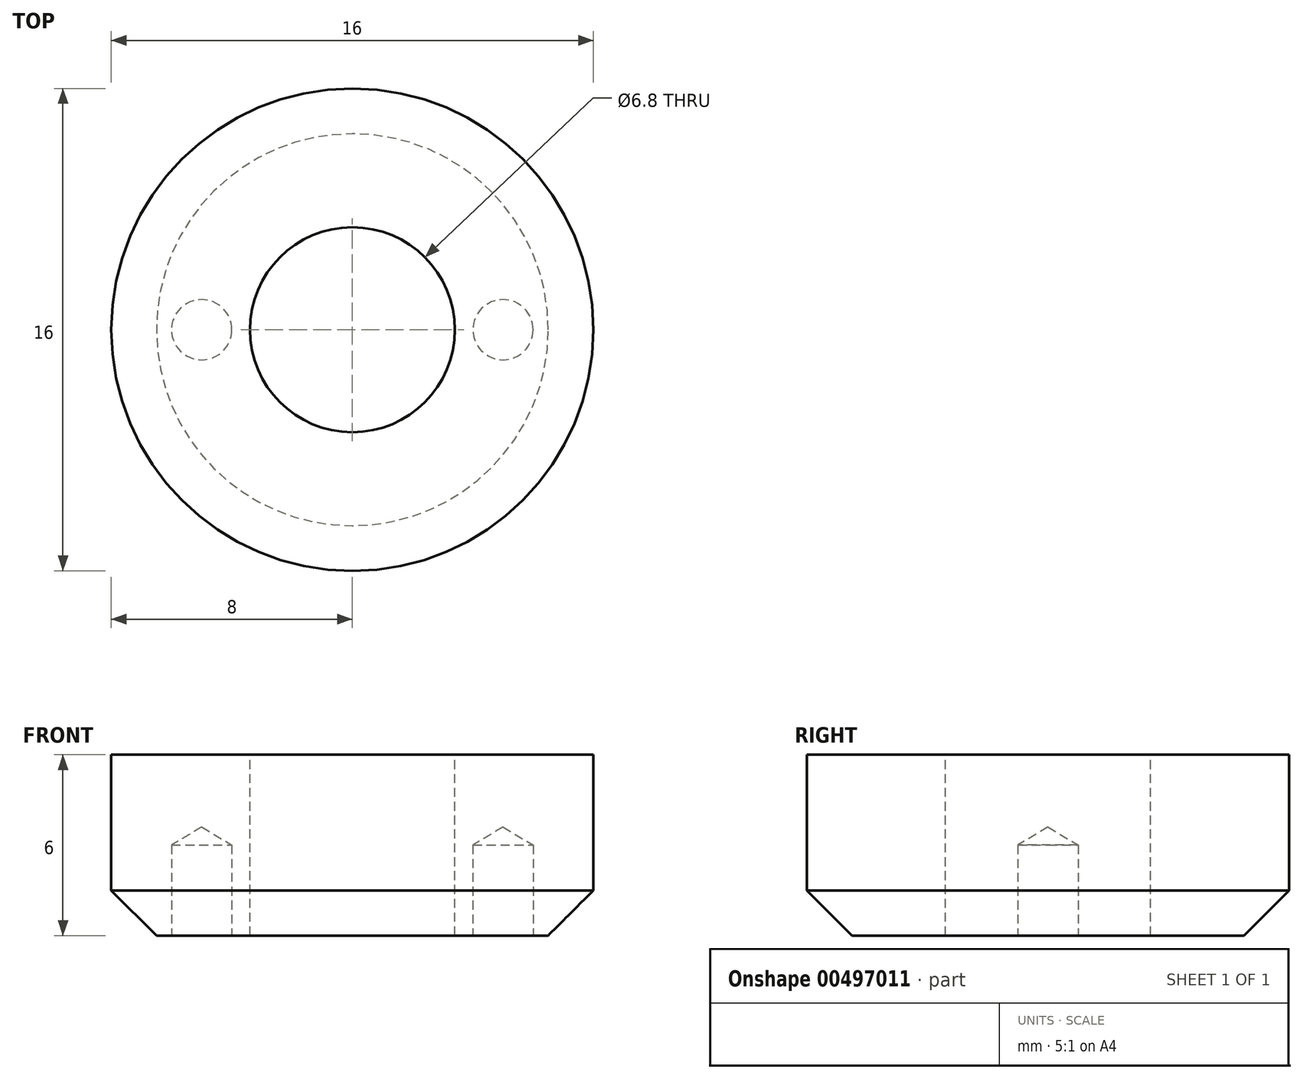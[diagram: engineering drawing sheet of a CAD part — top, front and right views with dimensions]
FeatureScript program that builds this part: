
annotation { "Feature Type Name" : "Feature", "Feature Type Description" : "" }
export const myFeature = defineFeature(function(context is Context, id is Id, definition is map)
    precondition{}
    {
        {
            var Q0;
            Q0=qCreatedBy(makeId("Top.planeOp"),FACE);
            var sketch = newSketch(context, id + "F0", { "sketchPlane" : qUnion([Q0])});
            skCircle(sketch, "E0", {"center": v(0, 0) * mm, "radius": 8 * mm});
            skSolve(sketch);
        }
        {
            var Q0;
            Q0=makeQuery(id+"F0.imprint","IMPRINT",FACE,{"disambiguationData":[TD([[makeQuery(id+"F0.imprint","IMPRINT",EDGE,{"derivedFrom":sQuery(id+"F0.wireOp",EDGE,"E0")}),1.0]])]});
            var sketch = newSketch(context, id + "F1", { "sketchPlane" : qUnion([Q0])});
            skCircle(sketch, "E1", {"center": v(0, 0) * mm, "radius": 2.36 * mm});
            skSolve(sketch);
        }
        {
            var Q0;
            Q0=makeQuery(id+"F0.imprint","IMPRINT",FACE,{"disambiguationData":[TD([[makeQuery(id+"F0.imprint","IMPRINT",EDGE,{"derivedFrom":sQuery(id+"F0.wireOp",EDGE,"E0")}),1.0]])]});
            extrude(context, id + "F2", {"entities" : qUnion([Q0]), "oppositeDirection" : true, "depth" : 6 * mm, "offsetDistance" : 25.4 * mm});
        }
        {
            var Q0;
            Q0=sQuery(id+"F1.wireOp",VERTEX,"E1.center");
            var Q1;
            Q1=makeQuery(id+"F2.opExtrude","SWEPT_BODY",BODY,{"disambiguationData":[OSD([sQuery(id+"F0.wireOp",EDGE,"E0")])]});
            hole(context, id + "F3", {"style" : HoleStyle.SIMPLE, "endStyle" : HoleEndStyle.BLIND, "standardTappedOrClearance" : lookupTablePath({ "standard" : "ISO", "engagement" : "75%", "pitch" : "1.25 mm", "size" : "M8", "type" : "Tapped" }), "standardBlindInLast" : lookupTablePath({ "standard" : "ISO", "engagement" : "75%", "pitch" : "1.25 mm", "size" : "M8", "type" : "Tapped" }), "holeDiameter" : 6.8 * mm, "majorDiameter" : 8 * mm, "showTappedDepth" : true, "holeDepth" : 13.9 * mm, "isTappedThrough" : true, "tappedDepth" : 10.15 * mm, "tapClearance" : 3, "startFromSketch" : true, "locations" : qUnion([Q0]), "scope" : qUnion([Q1])});
        }
        {
            var Q0;
            Q0=makeQuery(id+"F2.opExtrude","CAP_EDGE",EDGE,{"disambiguationData":[OSD([sQuery(id+"F0.wireOp",EDGE,"E0")])],"isStart":false});
            chamfer(context, id + "F4", {"entities" : qUnion([Q0]), "width" : 1.5 * mm, "tangentPropagation" : true});
        }
        {
            var Q0;
            Q0=makeQuery(id+"F2.opExtrude","CAP_FACE",FACE,{"disambiguationData":[OSD([sQuery(id+"F0.wireOp",EDGE,"E0")])],"isStart":false});
            var sketch = newSketch(context, id + "F5", { "sketchPlane" : qUnion([Q0])});
            skCircle(sketch, "E2", {"center": v(-5, 0) * mm, "radius": 0.75 * mm});
            skCircle(sketch, "E3", {"center": v(5, 0) * mm, "radius": 0.75 * mm});
            skSolve(sketch);
        }
        {
            var Q0;
            Q0=sQuery(id+"F5.wireOp",VERTEX,"E2.center");
            var Q1;
            Q1=sQuery(id+"F5.wireOp",VERTEX,"E3.center");
            var Q2;
            Q2=makeQuery(id+"F2.opExtrude","SWEPT_BODY",BODY,{"disambiguationData":[OSD([sQuery(id+"F0.wireOp",EDGE,"E0")])]});
            hole(context, id + "F6", {"style" : HoleStyle.SIMPLE, "endStyle" : HoleEndStyle.BLIND, "holeDiameter" : 2 * mm, "majorDiameter" : 8 * mm, "holeDepth" : 3 * mm, "isTappedThrough" : true, "tappedDepth" : 10.14 * mm, "tapClearance" : 3, "startFromSketch" : true, "locations" : qUnion([Q0, Q1]), "scope" : qUnion([Q2])});
        }
    });
